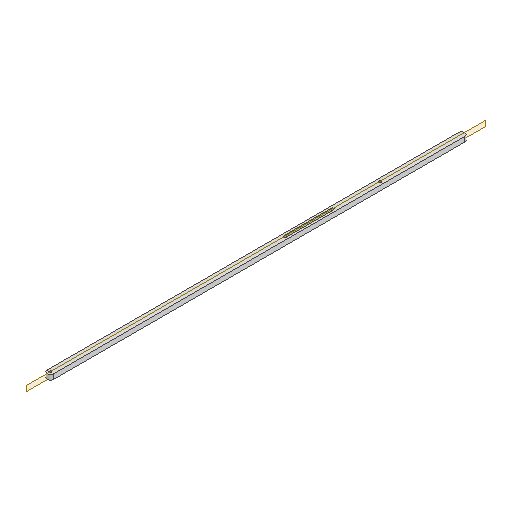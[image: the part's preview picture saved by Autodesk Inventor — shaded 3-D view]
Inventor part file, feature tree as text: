
AUTODESK INVENTOR PART (.ipt)
format: ipt  version: 2022 (Build 260153000, 153)  size: 123,904 bytes
history: native  units: mm
features: extrude x2, sketch x2, projected_geometry x1
ambient origin geometry x8: Origin, YZ Plane, XZ Plane, XY Plane, X Axis, Y Axis, Z Axis, Center Point
bodies: Solid1 (feature_tree)
feature tree (5):
  extrude  "Extrusion1"  Depth=405.743mm
  extrude  "Extrusion2"  Depth=3.0mm
  sketch  "Sketch1"  dims[d0=8.0mm d1=405.743mm]
  sketch  "Sketch2"  dims[d2=3.0mm d3=3.0mm d4=6.0mm d5=0.0mm d20=3.0mm d21=58.68mm d22=117.0mm d23=8.0mm d24=100.0mm d25=4.363323mm d26=4.363323mm d27=10.0mm d28=0.0mm]
  projected_geometry  "Projected Loop1"
